# Revit family: 1AHQM_DN40-50_External_RFA
name_source: partatom
category: Pipe Accessories
units: mm (PartAtom-declared; Revit-internal decimal feet)

## family parameters
Always vertical = Yes
Cut with Voids When Loaded = No
OmniClass Number = 23.65.55.14.17
OmniClass Title = Adjusting/Controlling Valves for Liquid Services
Part Type = Valve - Breaks Into
Round Connector Dimension = Use Diameter
Shared = No
Work Plane-Based = No

## types (2) — shared parameters
Connection = External Thread
Description = Pressure Independent Control Valve
H = 142 mm
H1 = 71 mm  [stored 0.23294 ft]
H2 = 35 mm  [stored 0.114829 ft]
HH = 141 mm  [stored 0.462598 ft]
H_B1 = 59 mm
H_B2 = 78 mm  [stored 0.255906 ft]
H_B3 = 79 mm
H_B4 = 16 mm  [stored 0.0524934 ft]
H_B5 = 28 mm  [stored 0.0918635 ft]
H_B6 = 12 mm  [stored 0.0393701 ft]
H_TP1 = 8 mm  [stored 0.0262467 ft]
IfcExportAs = IfcValveType
IfcExportType = AHQM
LOD 200 = No
LOD 350 = Yes
Manufacturer = Danfoss
Max Differential Pressure = 4 bar
Max Medium Temperature = 120 °C
Min Medium Temperature = 2 °C
Nominal Pressure = PN 16
R_B2 = 55 mm  [stored 0.180446 ft]
R_B3 = 51 mm
R_B4 = 40 mm  [stored 0.131234 ft]
R_B5 = 24 mm  [stored 0.0787402 ft]
R_B6 = 65 mm  [stored 0.213255 ft]
R_B7 = 30 mm  [stored 0.0984252 ft]
R_T1 = 30 mm  [stored 0.0984252 ft]
R_T2 = 33 mm  [stored 0.108268 ft]
Stroke = 10 mm
URL = https://store.danfoss.com
Valve Body Material = Danfoss Grey Iron

## per-type parameters (varying)
| type | D | H_TP2 | Kvs | L | L1 | L2 | L_TP1 | L_TP2 | Max Flow | Min Flow | Model | Model Type | R | R_B1 | R_V1 | R_V2 | R_V3 | TR | W_TP | Weight |
| AHQM_DN50_External_003L3602 | 50 mm  [stored 0.164042 ft] | 16 mm  [stored 0.0524934 ft] | 20.0 m³/h | 130 mm  [stored 0.426509 ft] | 21 mm  [stored 0.0688976 ft] | 13 mm | 26 mm | 26 mm | 12.5 m³/h | 2.5 m³/h | 003L3602 | AHQM_DN50_External | 38 mm  [stored 0.124672 ft] | 35 mm  [stored 0.114829 ft] | 44 mm  [stored 0.144357 ft] | 56 mm  [stored 0.183727 ft] | 47 mm  [stored 0.154199 ft] | 76 mm  [stored 0.249344 ft] | 58 mm  [stored 0.190289 ft] | 6.20 kg |
| AHQM_DN40_External_003L3601 | 40 mm  [stored 0.131234 ft] | 15 mm  [stored 0.0492126 ft] | 12.5 m³/h | 110 mm  [stored 0.360892 ft] | 18 mm  [stored 0.0590551 ft] | 8 mm  [stored 0.0262467 ft] | 20 mm  [stored 0.0656168 ft] | 20 mm  [stored 0.0656168 ft] | 7.5 m³/h | 1.5 m³/h | 003L3601 | AHQM_DN40_External | 30 mm  [stored 0.0984252 ft] | 33 mm  [stored 0.108268 ft] | 37 mm  [stored 0.121391 ft] | 49 mm  [stored 0.160761 ft] | 40 mm  [stored 0.131234 ft] | 60 mm  [stored 0.19685 ft] | 49 mm  [stored 0.160761 ft] | 5.40 kg |

note: [stored X ft] marks values corroborated as IEEE doubles in the binary element streams (Revit-internal decimal feet)

## geometry (parser evidence)
native form markers: Sweep x2
no freeform markers — native parametric forms only
